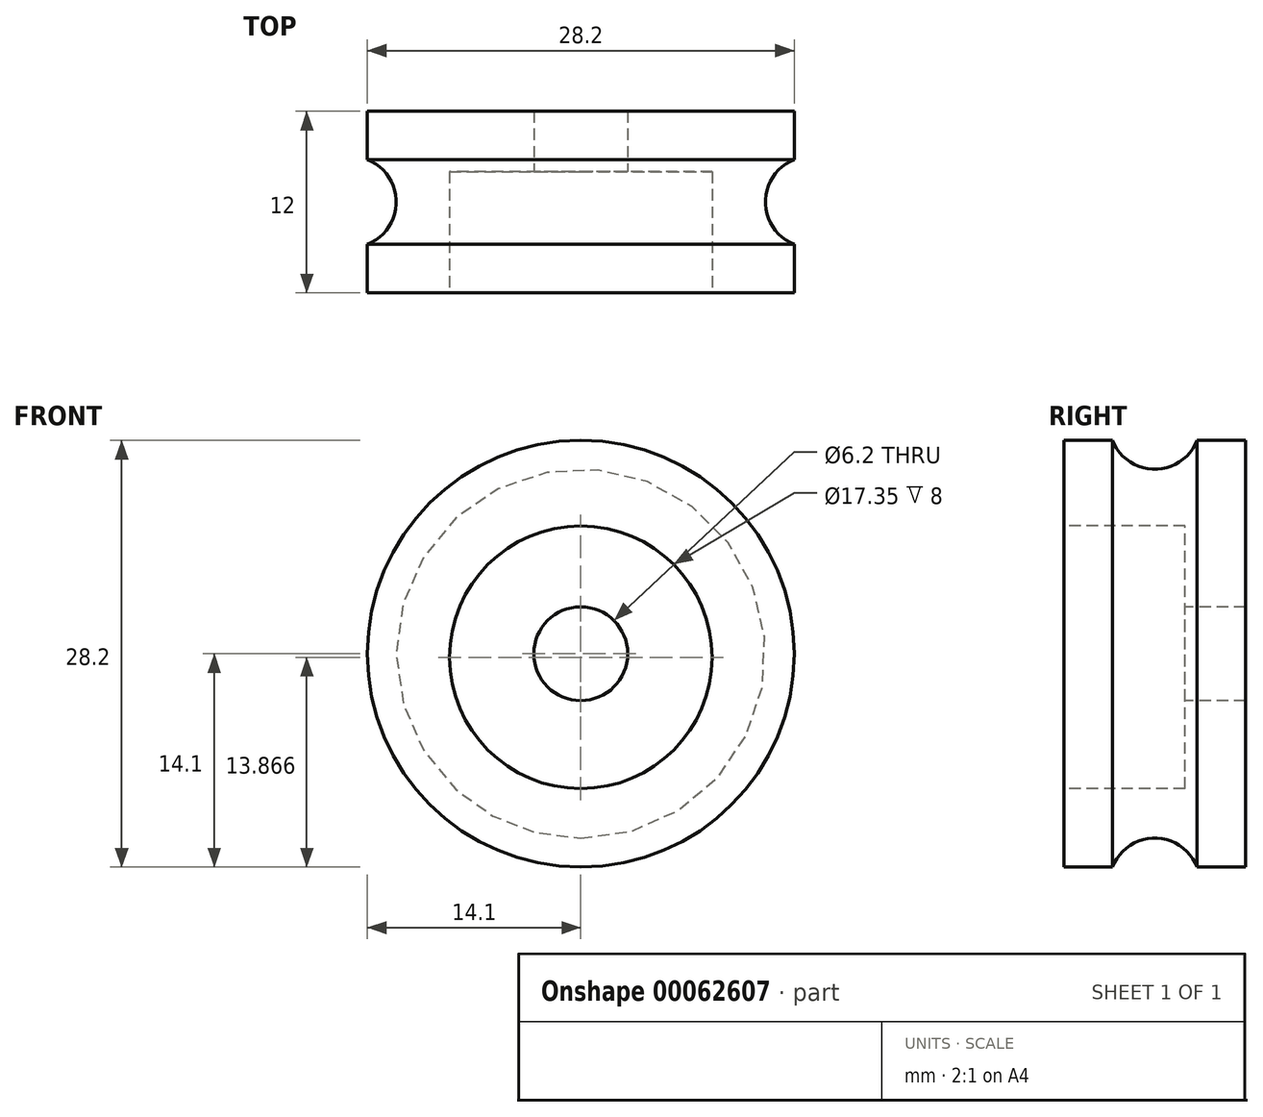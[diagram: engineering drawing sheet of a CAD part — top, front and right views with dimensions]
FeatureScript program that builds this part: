
annotation { "Feature Type Name" : "Feature", "Feature Type Description" : "" }
export const myFeature = defineFeature(function(context is Context, id is Id, definition is map)
    precondition{}
    {
        {
            var Q0;
            Q0=qCreatedBy(makeId("Right.planeOp"),FACE);
            var sketch = newSketch(context, id + "F0", { "sketchPlane" : qUnion([Q0])});
            skLineSegment(sketch, "E0", {"start": v(0, 0) * mm, "end": v(0, 3.1) * mm, "construction": true});
            skLineSegment(sketch, "E1", {"start": v(0, 3.1) * mm, "end": v(-6, 3.1) * mm});
            skLineSegment(sketch, "E2", {"start": v(-6, 3.1) * mm, "end": v(-6, 14.1) * mm});
            skLineSegment(sketch, "E3.MirrorCS", {"start": v(6, 3.1) * mm, "end": v(6, 14.1) * mm});
            skLineSegment(sketch, "E4.MirrorCS", {"start": v(0, 3.1) * mm, "end": v(6, 3.1) * mm});
            skLineSegment(sketch, "E5", {"start": v(-15.39, 0) * mm, "end": v(15.68, 0) * mm, "construction": true});
            skLineSegment(sketch, "E6", {"start": v(6, 14.1) * mm, "end": v(2.8, 14.1) * mm});
            skLineSegment(sketch, "E7.MirrorCS", {"start": v(-6, 14.1) * mm, "end": v(-2.8, 14.1) * mm});
            skLineSegment(sketch, "E8", {"start": v(0, 3.1) * mm, "end": v(0, 11.1) * mm, "construction": true});
            skArc(sketch, "E9", {"start": v(-2.8, 14.1) * mm, "mid": v(0, 12.2) * mm, "end": v(2.8, 14.1) * mm});
            skSolve(sketch);
        }
        {
            var Q0;
            Q0=makeQuery(id+"F0.imprint","IMPRINT",FACE,{"disambiguationData":[TD([[makeQuery(id+"F0.imprint","IMPRINT",EDGE,{"derivedFrom":sQuery(id+"F0.wireOp",EDGE,"E1")}),-1.0]])]});
            var Q1;
            Q1=sQuery(id+"F0.wireOp",EDGE,"E5");
            revolve(context, id + "F1", {"entities" : qUnion([Q0]), "axis" : qUnion([Q1]), "revolveType" : RevolveType.FULL});
        }
        {
            var Q0;
            Q0=makeQuery(id+"F1.opRevolve","SWEPT_FACE",FACE,{"disambiguationData":[OSD([sQuery(id+"F0.wireOp",EDGE,"E2")])]});
            var sketch = newSketch(context, id + "F2", { "sketchPlane" : qUnion([Q0])});
            skCircle(sketch, "E10", {"center": v(0, -0.23) * mm, "radius": 8.68 * mm});
            skSolve(sketch);
        }
        {
            var Q0;
            Q0=makeQuery(id+"F2.imprint","IMPRINT",FACE,{"disambiguationData":[TD([[makeQuery(id+"F2.imprint","IMPRINT",EDGE,{"derivedFrom":sQuery(id+"F2.wireOp",EDGE,"E10")}),1.0]])]});
            extrude(context, id + "F3", {"entities" : qUnion([Q0]), "operationType" : NewBodyOperationType.REMOVE, "oppositeDirection" : true, "depth" : 8 * mm});
        }
    });
